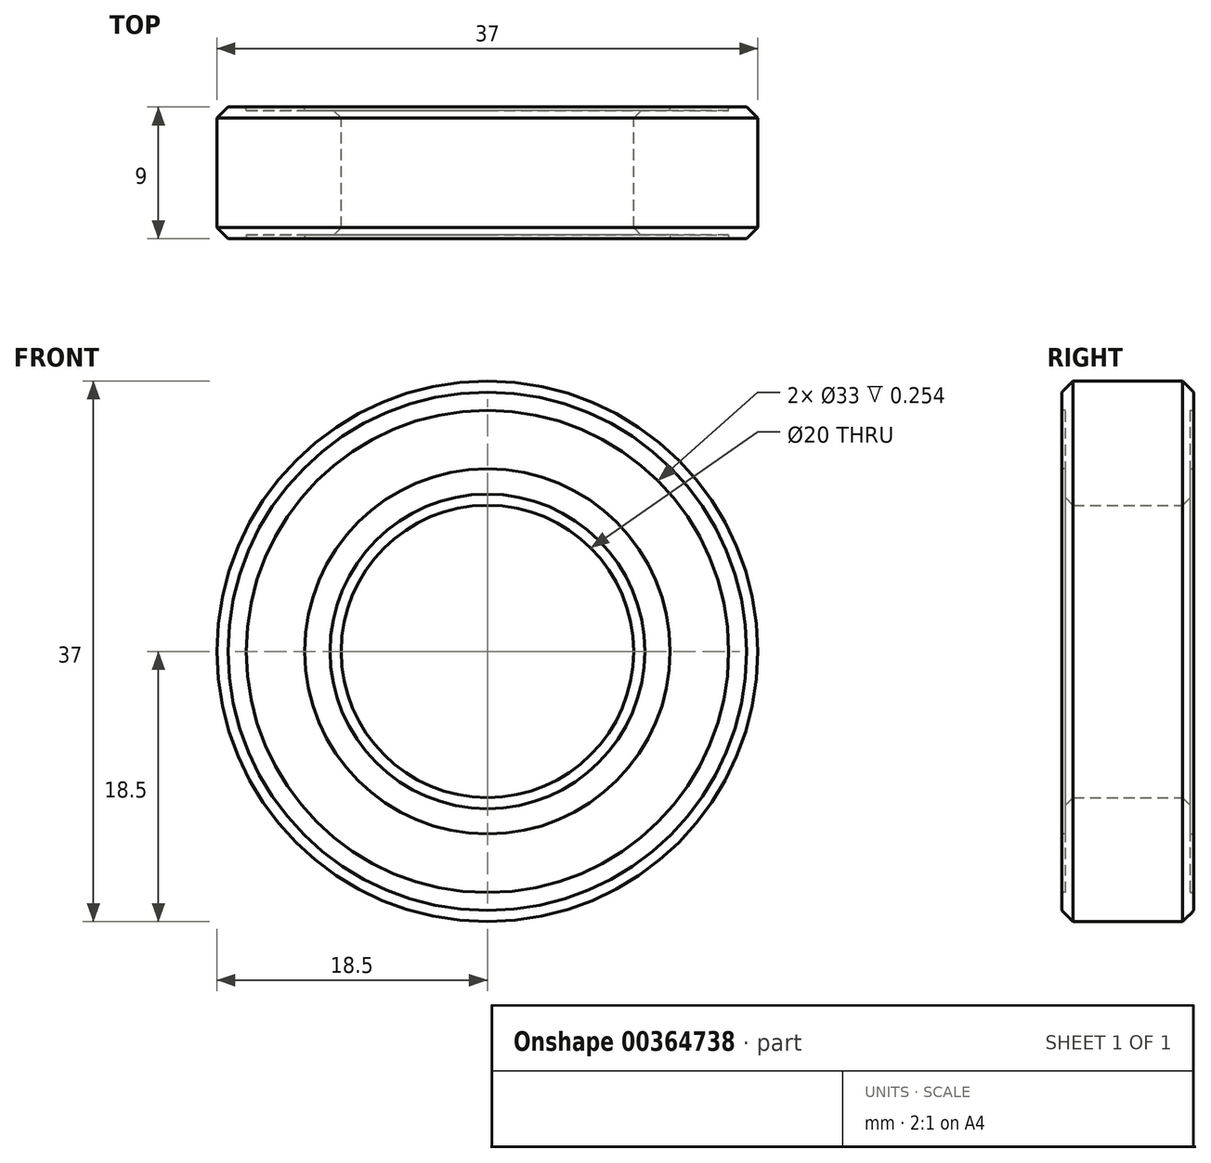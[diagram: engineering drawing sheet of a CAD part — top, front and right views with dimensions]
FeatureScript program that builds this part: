
annotation { "Feature Type Name" : "Feature", "Feature Type Description" : "" }
export const myFeature = defineFeature(function(context is Context, id is Id, definition is map)
    precondition{}
    {
        {
            var Q0;
            Q0=qCreatedBy(makeId("Front.planeOp"),FACE);
            var sketch = newSketch(context, id + "F0", { "sketchPlane" : qUnion([Q0])});
            skCircle(sketch, "E0", {"center": v(0, 0) * mm, "radius": 10 * mm});
            skCircle(sketch, "E1", {"center": v(0, 0) * mm, "radius": 18.5 * mm});
            skSolve(sketch);
        }
        {
            var Q0;
            Q0 = qSketchRegion(id + "F0", true);
            extrude(context, id + "F1", {"entities" : qUnion([Q0]), "depth" : 9 * mm});
        }
        {
            var Q0;
            Q0=makeQuery(id+"F1.opExtrude","SWEPT_FACE",FACE,{"disambiguationData":[OSD([sQuery(id+"F0.wireOp",EDGE,"E1")])]});
            var Q1;
            Q1=makeQuery(id+"F1.opExtrude","SWEPT_FACE",FACE,{"disambiguationData":[OSD([sQuery(id+"F0.wireOp",EDGE,"E0")])]});
            chamfer(context, id + "F2", {"entities" : qUnion([Q0, Q1]), "width" : 0.76 * mm, "tangentPropagation" : true});
        }
        {
            var Q0;
            Q0=makeQuery(id+"F1.opExtrude","CAP_FACE",FACE,{"disambiguationData":[OSD([sQuery(id+"F0.wireOp",EDGE,"E0"),sQuery(id+"F0.wireOp",EDGE,"E1")])],"isStart":false});
            var sketch = newSketch(context, id + "F3", { "sketchPlane" : qUnion([Q0])});
            skCircle(sketch, "E2", {"center": v(0, 0) * mm, "radius": 12.5 * mm});
            skCircle(sketch, "E3", {"center": v(0, 0) * mm, "radius": 16.5 * mm});
            skSolve(sketch);
        }
        {
            var Q0;
            Q0 = qSketchRegion(id + "F3", true);
            extrude(context, id + "F4", {"entities" : qUnion([Q0]), "operationType" : NewBodyOperationType.REMOVE, "oppositeDirection" : true, "depth" : 0.25 * mm});
        }
        {
            var Q0;
            Q0=makeQuery(id+"F1.opExtrude","CAP_FACE",FACE,{"disambiguationData":[OSD([sQuery(id+"F0.wireOp",EDGE,"E0"),sQuery(id+"F0.wireOp",EDGE,"E1")])],"isStart":true});
            var sketch = newSketch(context, id + "F5", { "sketchPlane" : qUnion([Q0])});
            skCircle(sketch, "E4", {"center": v(0, 0) * mm, "radius": 12.5 * mm});
            skCircle(sketch, "E5", {"center": v(0, 0) * mm, "radius": 16.5 * mm});
            skSolve(sketch);
        }
        {
            var Q0;
            Q0 = qSketchRegion(id + "F5", true);
            extrude(context, id + "F6", {"entities" : qUnion([Q0]), "operationType" : NewBodyOperationType.REMOVE, "oppositeDirection" : true, "depth" : 0.25 * mm});
        }
    });
